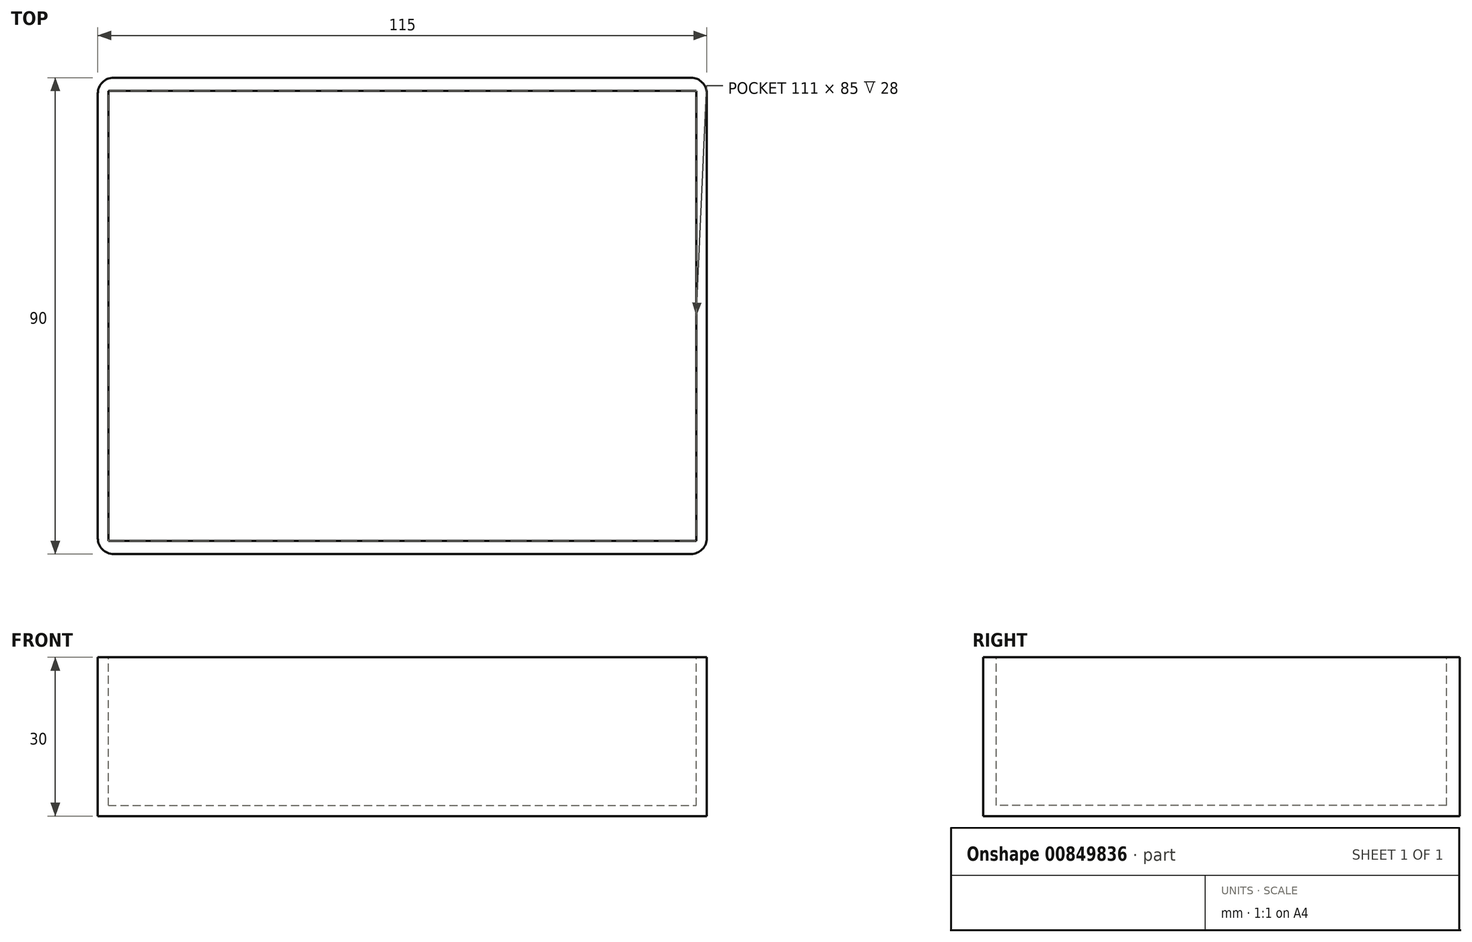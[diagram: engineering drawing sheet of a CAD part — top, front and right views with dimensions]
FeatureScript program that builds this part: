
annotation { "Feature Type Name" : "Feature", "Feature Type Description" : "" }
export const myFeature = defineFeature(function(context is Context, id is Id, definition is map)
    precondition{}
    {
        {
            var Q0;
            Q0=qCreatedBy(makeId("Top.planeOp"),FACE);
            var sketch = newSketch(context, id + "F0", { "sketchPlane" : qUnion([Q0])});
            skLineSegment(sketch, "E0.bottom", {"start": v(-57.5, 45) * mm, "end": v(57.5, 45) * mm});
            skLineSegment(sketch, "E0.top", {"start": v(-57.5, -45) * mm, "end": v(57.5, -45) * mm});
            skLineSegment(sketch, "E0.left", {"start": v(-57.5, 45) * mm, "end": v(-57.5, -45) * mm});
            skLineSegment(sketch, "E0.right", {"start": v(57.5, 45) * mm, "end": v(57.5, -45) * mm});
            skPoint(sketch, "E0.middle", {"position": v(0, 0) * mm});
            skSolve(sketch);
        }
        {
            var Q0;
            Q0=makeQuery(id+"F0.imprint","IMPRINT",FACE,{"disambiguationData":[TD([[makeQuery(id+"F0.imprint","IMPRINT",EDGE,{"derivedFrom":sQuery(id+"F0.wireOp",EDGE,"E0.bottom")}),-1.0]])]});
            var Q1;
            Q1=makeQuery(id+"F0.imprint","IMPRINT",FACE,{"disambiguationData":[TD([[makeQuery(id+"F0.imprint","IMPRINT",EDGE,{"derivedFrom":sQuery(id+"F0.wireOp",EDGE,"42d2a5ed-0d50-467e-a08a-62517fd30f35.0")}),-1.0]])]});
            extrude(context, id + "F1", {"entities" : qUnion([Q0, Q1]), "depth" : 30 * mm, "offsetDistance" : 25 * mm});
        }
        {
            var Q0;
            Q0=makeQuery(id+"F1.opExtrude","CAP_FACE",FACE,{"disambiguationData":[OSD([sQuery(id+"F0.wireOp",EDGE,"E0.bottom"),sQuery(id+"F0.wireOp",EDGE,"E0.top"),sQuery(id+"F0.wireOp",EDGE,"E0.left"),sQuery(id+"F0.wireOp",EDGE,"E0.right")])],"isStart":false});
            cPlane(context, id + "F2", {"entities" : qUnion([Q0]), "cplaneType" : CPlaneType.OFFSET, "offset" : 0 * mm, "oppositeDirection" : true, "width" : 150 * mm, "height" : 150 * mm});
        }
        {
            var Q0;
            Q0=qCreatedBy(id+"F2.planeOp",FACE);
            var sketch = newSketch(context, id + "F3", { "sketchPlane" : qUnion([Q0])});
            skLineSegment(sketch, "E1.bottom", {"start": v(-55.5, 42.5) * mm, "end": v(55.5, 42.5) * mm});
            skLineSegment(sketch, "E1.top", {"start": v(-55.5, -42.5) * mm, "end": v(55.5, -42.5) * mm});
            skLineSegment(sketch, "E1.left", {"start": v(-55.5, 42.5) * mm, "end": v(-55.5, -42.5) * mm});
            skLineSegment(sketch, "E1.right", {"start": v(55.5, 42.5) * mm, "end": v(55.5, -42.5) * mm});
            skPoint(sketch, "E1.middle", {"position": v(0, 0) * mm});
            skSolve(sketch);
        }
        {
            var Q0;
            Q0 = qSketchRegion(id + "F3", true);
            extrude(context, id + "F4", {"entities" : qUnion([Q0]), "operationType" : NewBodyOperationType.REMOVE, "oppositeDirection" : true, "depth" : 28 * mm, "offsetDistance" : 25 * mm});
        }
        {
            var Q0;
            Q0=makeQuery(id+"F1.opExtrude","SWEPT_EDGE",EDGE,{"disambiguationData":[OSD([sQuery(id+"F0.wireOp",EDGE,"E0.bottom"),sQuery(id+"F0.wireOp",EDGE,"E0.left")])]});
            var Q1;
            Q1=makeQuery(id+"F1.opExtrude","SWEPT_EDGE",EDGE,{"disambiguationData":[OSD([sQuery(id+"F0.wireOp",EDGE,"E0.bottom"),sQuery(id+"F0.wireOp",EDGE,"E0.right")])]});
            var Q2;
            Q2=makeQuery(id+"F1.opExtrude","SWEPT_EDGE",EDGE,{"disambiguationData":[OSD([sQuery(id+"F0.wireOp",EDGE,"E0.top"),sQuery(id+"F0.wireOp",EDGE,"E0.right")])]});
            var Q3;
            Q3=makeQuery(id+"F1.opExtrude","SWEPT_EDGE",EDGE,{"disambiguationData":[OSD([sQuery(id+"F0.wireOp",EDGE,"E0.top"),sQuery(id+"F0.wireOp",EDGE,"E0.left")])]});
            fillet(context, id + "F5", {"entities" : qUnion([Q0, Q1, Q2, Q3]), "radius" : 3 * mm, "tangentPropagation" : true, "allowEdgeOverflow" : false});
        }
    });
